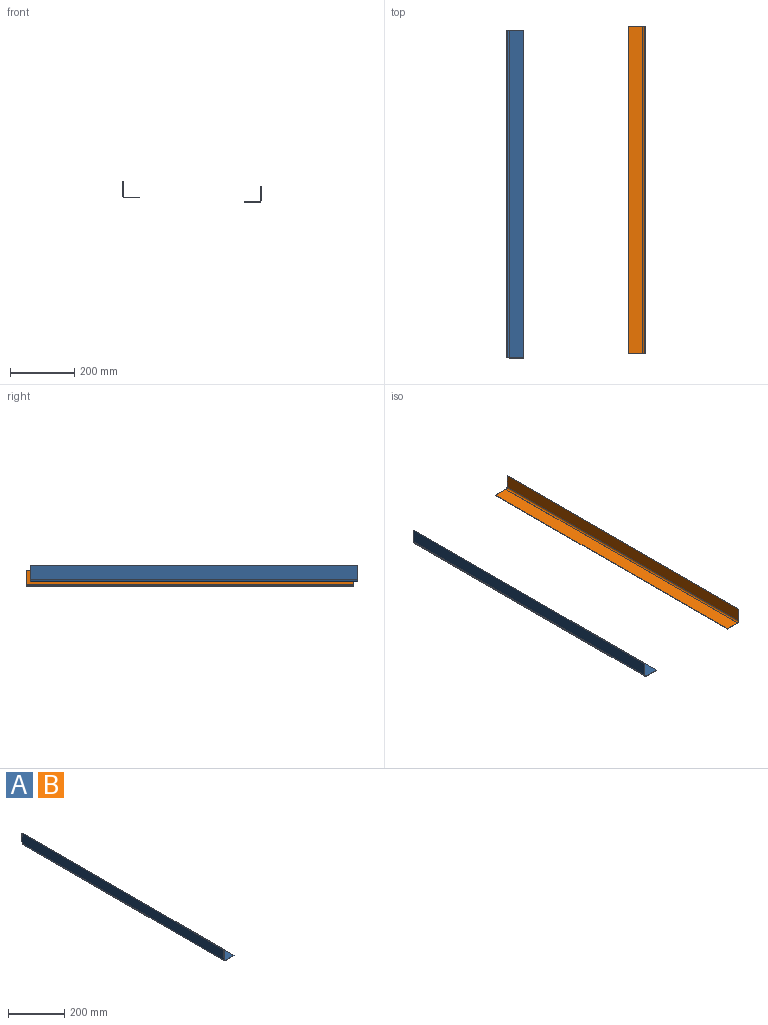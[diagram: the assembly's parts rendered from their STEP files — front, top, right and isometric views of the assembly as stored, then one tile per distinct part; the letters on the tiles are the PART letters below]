
ASSEMBLY  parts=2 mates=2
PART A: 10 faces, bbox 50.8x1016x50.8 mm
  f0: plane 1016x44.45mm, normal (-1,0,0), area 45161.2mm2, adj f5,f6,f7,f9
  f1: plane 1016x44.45mm, normal (0,0,-1), area 45161.2mm2, adj f2,f6,f7,f9
  f2: plane 1016x1.59mm, normal (1,0,0), area 1612.9mm2, adj f1,f3,f6,f7
  f3: plane 1016x44.13mm, normal (0,0,1), area 44838.6mm2, adj f2,f6,f7,f8
  f4: plane 1016x44.13mm, normal (1,0,0), area 44838.6mm2, adj f5,f6,f7,f8
  f5: plane 1016x1.59mm, normal (0,0,1), area 1612.9mm2, adj f0,f4,f6,f7
  f6: plane 50.8x50.8mm, normal (0,1,0), area 155.7mm2, adj f0,f1,f2,f3,f4,f5,f8,f9
  f7: plane 50.8x50.8mm, normal (0,-1,0), area 155.7mm2, adj f0,f1,f2,f3,f4,f5,f8,f9
  f8: cylinder r=5.08mm len=1016mm, axis (0,-1,0), area 8107.3mm2, adj f3,f4,f6,f7
  f9: cylinder r=6.35mm len=1016mm, axis (0,1,0), area 10134.1mm2, adj f0,f1,f6,f7
PART B: same geometry as A
PLACE A rot(axis=(0,0,1),0deg) t=(-56.71,-1005.07,317.51)mm
PLACE B rot(axis=(0,0,1),180deg) t=(371.98,25.81,303.94)mm
MATE parallel A.f7 <-> B.f6  axis (0,-1,0) through (-43.14,-1005.07,331.08)mm
MATE parallel A.f4 <-> B.f4  axis (1,0,0) through (-55.13,-497.07,368.31)mm
